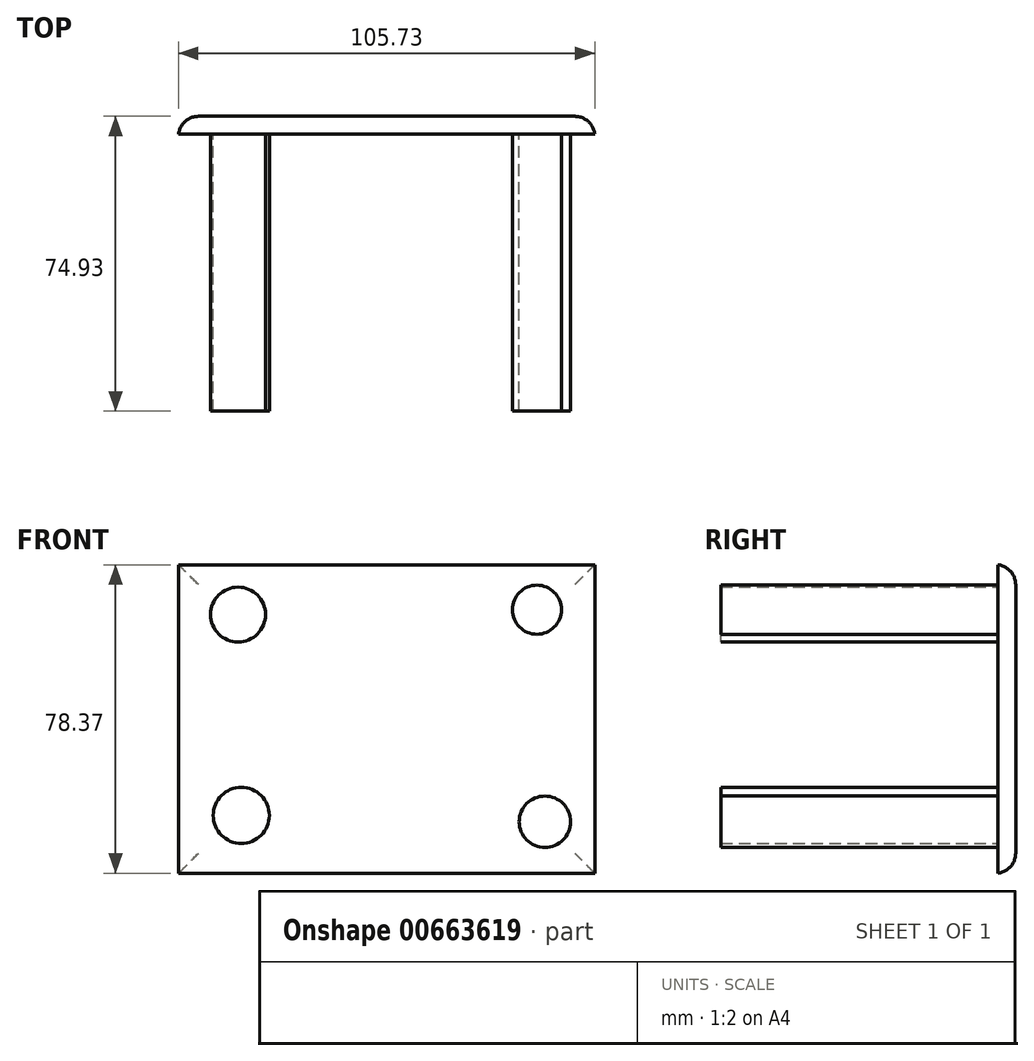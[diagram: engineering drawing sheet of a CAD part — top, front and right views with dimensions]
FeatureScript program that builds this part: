
annotation { "Feature Type Name" : "Feature", "Feature Type Description" : "" }
export const myFeature = defineFeature(function(context is Context, id is Id, definition is map)
    precondition{}
    {
        {
            var Q0;
            Q0=qCreatedBy(makeId("Front.planeOp"),FACE);
            var sketch = newSketch(context, id + "F0", { "sketchPlane" : qUnion([Q0])});
            skLineSegment(sketch, "E0.bottom", {"start": v(-26.53, 12.45) * mm, "end": v(75.52, 12.45) * mm});
            skLineSegment(sketch, "E0.top", {"start": v(-26.53, -55.31) * mm, "end": v(75.52, -55.31) * mm});
            skLineSegment(sketch, "E0.left", {"start": v(-26.53, 12.45) * mm, "end": v(-26.53, -55.31) * mm});
            skLineSegment(sketch, "E0.right", {"start": v(75.52, 12.45) * mm, "end": v(75.52, -55.31) * mm});
            skCircle(sketch, "E1", {"center": v(-14.7, 3.88) * mm, "radius": 6.98 * mm});
            skCircle(sketch, "E2", {"center": v(61.23, 5.1) * mm, "radius": 6.23 * mm});
            skCircle(sketch, "E3", {"center": v(63.27, -48.78) * mm, "radius": 6.53 * mm});
            skCircle(sketch, "E4", {"center": v(-13.88, -47.15) * mm, "radius": 7.13 * mm});
            skSolve(sketch);
        }
        {
            var Q0;
            Q0=makeQuery(id+"F0.imprint","IMPRINT",FACE,{"disambiguationData":[TD([[makeQuery(id+"F0.imprint","IMPRINT",EDGE,{"derivedFrom":sQuery(id+"F0.wireOp",EDGE,"E1")}),1.0]])]});
            var Q1;
            Q1=makeQuery(id+"F0.imprint","IMPRINT",FACE,{"disambiguationData":[TD([[makeQuery(id+"F0.imprint","IMPRINT",EDGE,{"derivedFrom":sQuery(id+"F0.wireOp",EDGE,"E4")}),1.0]])]});
            var Q2;
            Q2=makeQuery(id+"F0.imprint","IMPRINT",FACE,{"disambiguationData":[TD([[makeQuery(id+"F0.imprint","IMPRINT",EDGE,{"derivedFrom":sQuery(id+"F0.wireOp",EDGE,"E2")}),1.0]])]});
            var Q3;
            Q3=makeQuery(id+"F0.imprint","IMPRINT",FACE,{"disambiguationData":[TD([[makeQuery(id+"F0.imprint","IMPRINT",EDGE,{"derivedFrom":sQuery(id+"F0.wireOp",EDGE,"E3")}),1.0]])]});
            extrude(context, id + "F1", {"entities" : qUnion([Q0, Q1, Q2, Q3]), "depth" : 70.36 * mm, "offsetDistance" : 25.4 * mm});
        }
        {
            var Q0;
            Q0=qCreatedBy(makeId("Front.planeOp"),FACE);
            var sketch = newSketch(context, id + "F2", { "sketchPlane" : qUnion([Q0])});
            skLineSegment(sketch, "E5.bottom", {"start": v(75.93, 16.53) * mm, "end": v(-29.8, 16.53) * mm});
            skLineSegment(sketch, "E5.top", {"start": v(75.93, -61.84) * mm, "end": v(-29.8, -61.84) * mm});
            skLineSegment(sketch, "E5.left", {"start": v(75.93, 16.53) * mm, "end": v(75.93, -61.84) * mm});
            skLineSegment(sketch, "E5.right", {"start": v(-29.8, 16.53) * mm, "end": v(-29.8, -61.84) * mm});
            skSolve(sketch);
        }
        {
            var Q0;
            Q0=makeQuery(id+"F2.imprint","IMPRINT",FACE,{"disambiguationData":[TD([[makeQuery(id+"F2.imprint","IMPRINT",EDGE,{"derivedFrom":sQuery(id+"F2.wireOp",EDGE,"E5.bottom")}),1.0]])]});
            extrude(context, id + "F3", {"entities" : qUnion([Q0]), "oppositeDirection" : true, "depth" : 4.57 * mm, "offsetDistance" : 25.4 * mm});
        }
        {
            var Q0;
            Q0=makeQuery(id+"F3.opExtrude","CAP_EDGE",EDGE,{"disambiguationData":[OSD([sQuery(id+"F2.wireOp",EDGE,"E5.bottom")])],"isStart":false});
            var Q1;
            Q1=makeQuery(id+"F3.opExtrude","CAP_FACE",FACE,{"disambiguationData":[OSD([sQuery(id+"F2.wireOp",EDGE,"E5.bottom"),sQuery(id+"F2.wireOp",EDGE,"E5.top"),sQuery(id+"F2.wireOp",EDGE,"E5.left"),sQuery(id+"F2.wireOp",EDGE,"E5.right")])],"isStart":false});
            fillet(context, id + "F4", {"entities" : qUnion([Q0, Q1]), "radius" : 5.08 * mm, "tangentPropagation" : true, "allowEdgeOverflow" : false});
        }
    });
